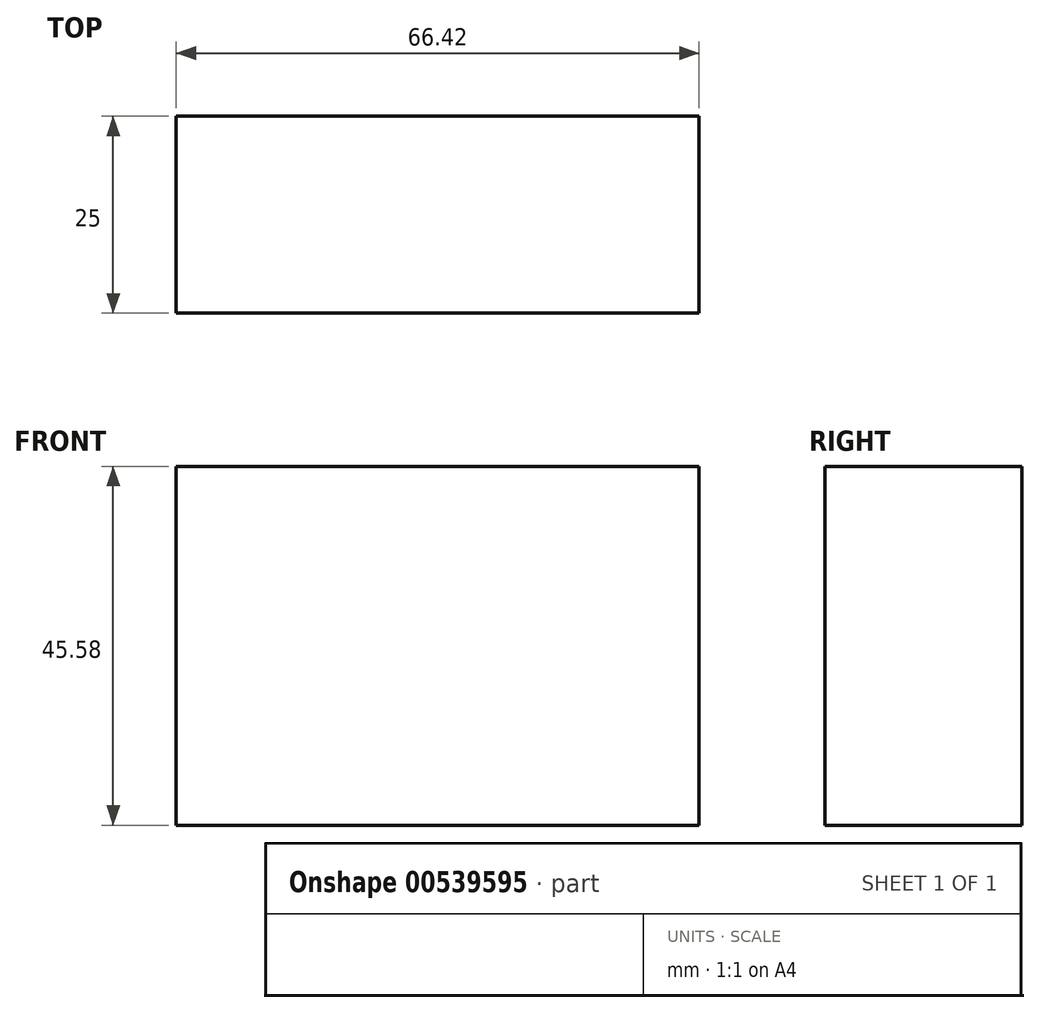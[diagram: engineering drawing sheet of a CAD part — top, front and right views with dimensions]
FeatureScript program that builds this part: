
annotation { "Feature Type Name" : "Feature", "Feature Type Description" : "" }
export const myFeature = defineFeature(function(context is Context, id is Id, definition is map)
    precondition{}
    {
        {
            var Q0;
            Q0=qCreatedBy(makeId("Front.planeOp"),FACE);
            var sketch = newSketch(context, id + "F0", { "sketchPlane" : qUnion([Q0])});
            skLineSegment(sketch, "E0.bottom", {"start": v(-115.82, 19.3) * mm, "end": v(-49.4, 19.3) * mm});
            skLineSegment(sketch, "E0.top", {"start": v(-115.82, -26.28) * mm, "end": v(-49.4, -26.28) * mm});
            skLineSegment(sketch, "E0.left", {"start": v(-115.82, 19.3) * mm, "end": v(-115.82, -26.28) * mm});
            skLineSegment(sketch, "E0.right", {"start": v(-49.4, 19.3) * mm, "end": v(-49.4, -26.28) * mm});
            skSolve(sketch);
        }
        {
            var Q0;
            Q0 = qSketchRegion(id + "F0", true);
            extrude(context, id + "F1", {"entities" : qUnion([Q0]), "depth" : 25 * mm, "offsetDistance" : 25 * mm});
        }
    });
